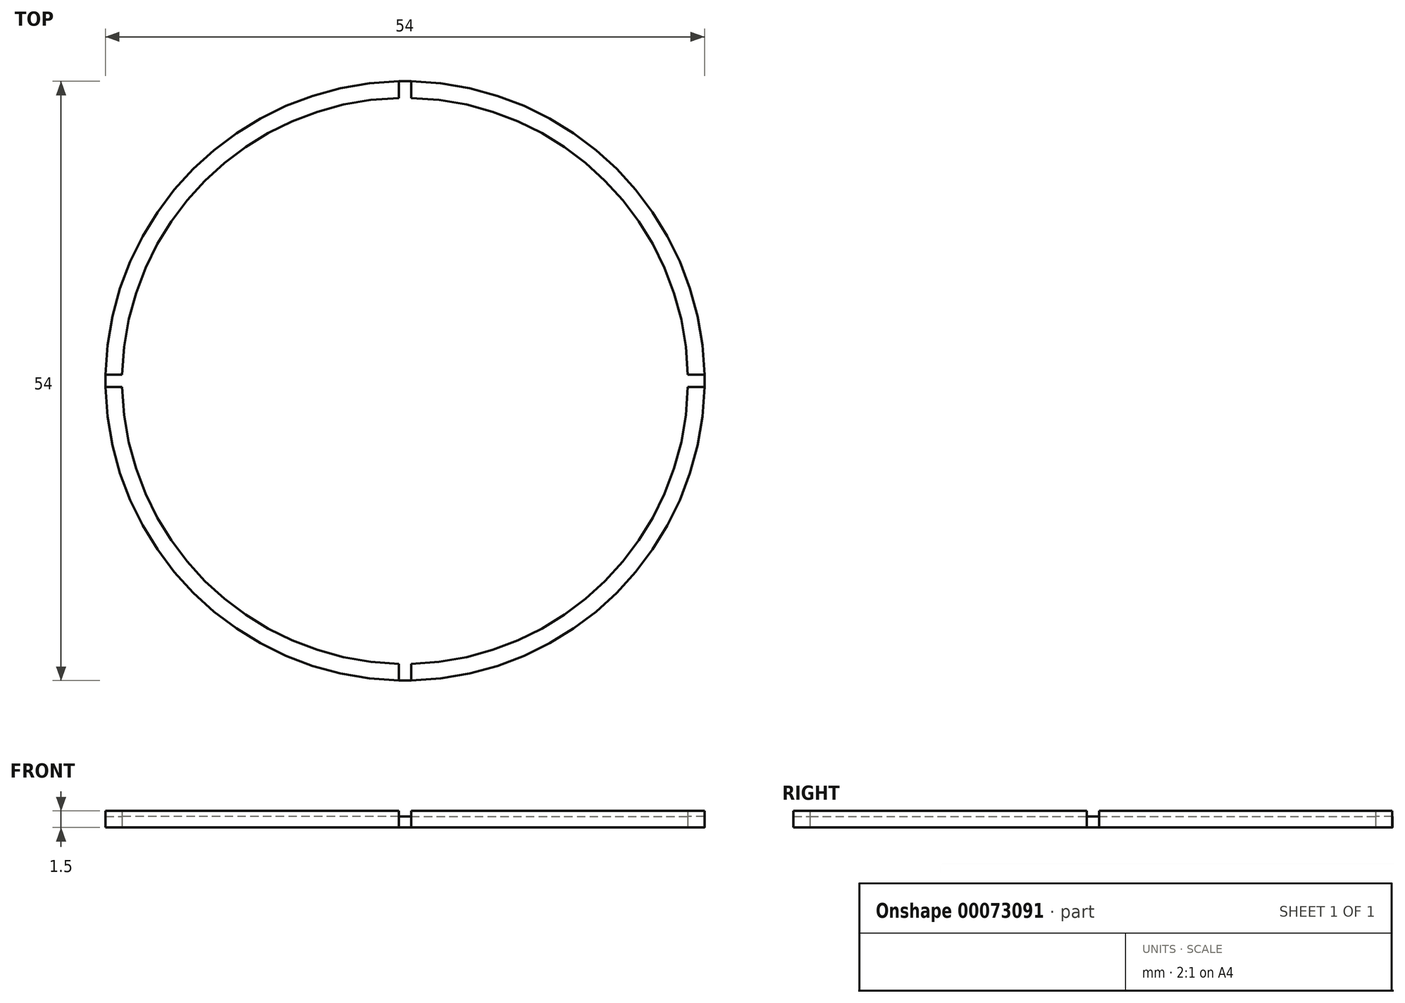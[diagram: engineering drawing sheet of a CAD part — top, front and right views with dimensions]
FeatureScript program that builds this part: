
annotation { "Feature Type Name" : "Feature", "Feature Type Description" : "" }
export const myFeature = defineFeature(function(context is Context, id is Id, definition is map)
    precondition{}
    {
        {
            var Q0;
            Q0=qCreatedBy(makeId("Top.planeOp"),FACE);
            var sketch = newSketch(context, id + "F0", { "sketchPlane" : qUnion([Q0])});
            skCircle(sketch, "E0", {"center": v(0, 0) * mm, "radius": 27 * mm});
            skCircle(sketch, "E1", {"center": v(0, 0) * mm, "radius": 25.5 * mm});
            skLineSegment(sketch, "E2", {"start": v(-27, 0.55) * mm, "end": v(-25.5, 0.55) * mm});
            skLineSegment(sketch, "E3", {"start": v(-27, -0.55) * mm, "end": v(-25.5, -0.55) * mm});
            skLineSegment(sketch, "E4", {"start": v(0.55, 27) * mm, "end": v(0.55, 25.5) * mm});
            skLineSegment(sketch, "E5", {"start": v(-0.55, 27) * mm, "end": v(-0.55, 25.5) * mm});
            skLineSegment(sketch, "E6", {"start": v(27, 0.55) * mm, "end": v(25.5, 0.55) * mm});
            skLineSegment(sketch, "E7", {"start": v(27, -0.55) * mm, "end": v(25.5, -0.55) * mm});
            skLineSegment(sketch, "E8", {"start": v(0.55, -27) * mm, "end": v(0.55, -25.5) * mm});
            skLineSegment(sketch, "E9", {"start": v(-0.55, -27) * mm, "end": v(-0.55, -25.5) * mm});
            skSolve(sketch);
        }
        {
            var Q0;
            {var subQ0=sQuery(id+"F0.wireOp",EDGE,"E3");Q0=makeQuery(id+"F0.imprint","IMPRINT",FACE,{"disambiguationData":[TD([[makeQuery(id+"F0.imprint","IMPRINT",EDGE,{"derivedFrom":subQ0}),-1.0]])]});}
            var Q1;
            {var subQ0=sQuery(id+"F0.wireOp",EDGE,"E7");Q1=makeQuery(id+"F0.imprint","IMPRINT",FACE,{"disambiguationData":[TD([[makeQuery(id+"F0.imprint","IMPRINT",EDGE,{"derivedFrom":subQ0}),1.0]])]});}
            var Q2;
            {var subQ0=sQuery(id+"F0.wireOp",EDGE,"E4");Q2=makeQuery(id+"F0.imprint","IMPRINT",FACE,{"disambiguationData":[TD([[makeQuery(id+"F0.imprint","IMPRINT",EDGE,{"derivedFrom":subQ0}),1.0]])]});}
            var Q3;
            {var subQ0=sQuery(id+"F0.wireOp",EDGE,"E2");Q3=makeQuery(id+"F0.imprint","IMPRINT",FACE,{"disambiguationData":[TD([[makeQuery(id+"F0.imprint","IMPRINT",EDGE,{"derivedFrom":subQ0}),1.0]])]});}
            extrude(context, id + "F1", {"entities" : qUnion([Q0, Q1, Q2, Q3]), "depth" : 1.5 * mm});
        }
        {
            var Q0;
            {var subQ0=sQuery(id+"F0.wireOp",EDGE,"E8");Q0=makeQuery(id+"F0.imprint","IMPRINT",FACE,{"disambiguationData":[TD([[makeQuery(id+"F0.imprint","IMPRINT",EDGE,{"derivedFrom":subQ0}),1.0]])]});}
            var Q1;
            {var subQ0=sQuery(id+"F0.wireOp",EDGE,"E1");var subQ4=makeQuery(id+"F0.imprint","INTERSECT",VERTEX,{"derivedFrom":[subQ0,sQuery(id+"F0.wireOp",EDGE,"E4")]});Q1=makeQuery(id+"F0.imprint","IMPRINT",FACE,{"disambiguationData":[TD([[makeQuery(id+"F0.imprint","IMPRINT",EDGE,{"disambiguationData":[TD([[subQ4,1.0]])],"derivedFrom":subQ0}),1.0]])]});}
            var Q2;
            {var subQ0=sQuery(id+"F0.wireOp",EDGE,"E6");Q2=makeQuery(id+"F0.imprint","IMPRINT",FACE,{"disambiguationData":[TD([[makeQuery(id+"F0.imprint","IMPRINT",EDGE,{"derivedFrom":subQ0}),1.0]])]});}
            var Q3;
            {var subQ0=sQuery(id+"F0.wireOp",EDGE,"E4");Q3=makeQuery(id+"F0.imprint","IMPRINT",FACE,{"disambiguationData":[TD([[makeQuery(id+"F0.imprint","IMPRINT",EDGE,{"derivedFrom":subQ0}),-1.0]])]});}
            var Q4;
            {var subQ0=sQuery(id+"F0.wireOp",EDGE,"E2");Q4=makeQuery(id+"F0.imprint","IMPRINT",FACE,{"disambiguationData":[TD([[makeQuery(id+"F0.imprint","IMPRINT",EDGE,{"derivedFrom":subQ0}),-1.0]])]});}
            extrude(context, id + "F2", {"entities" : qUnion([Q0, Q1, Q2, Q3, Q4]), "depth" : 1 * mm});
        }
    });
